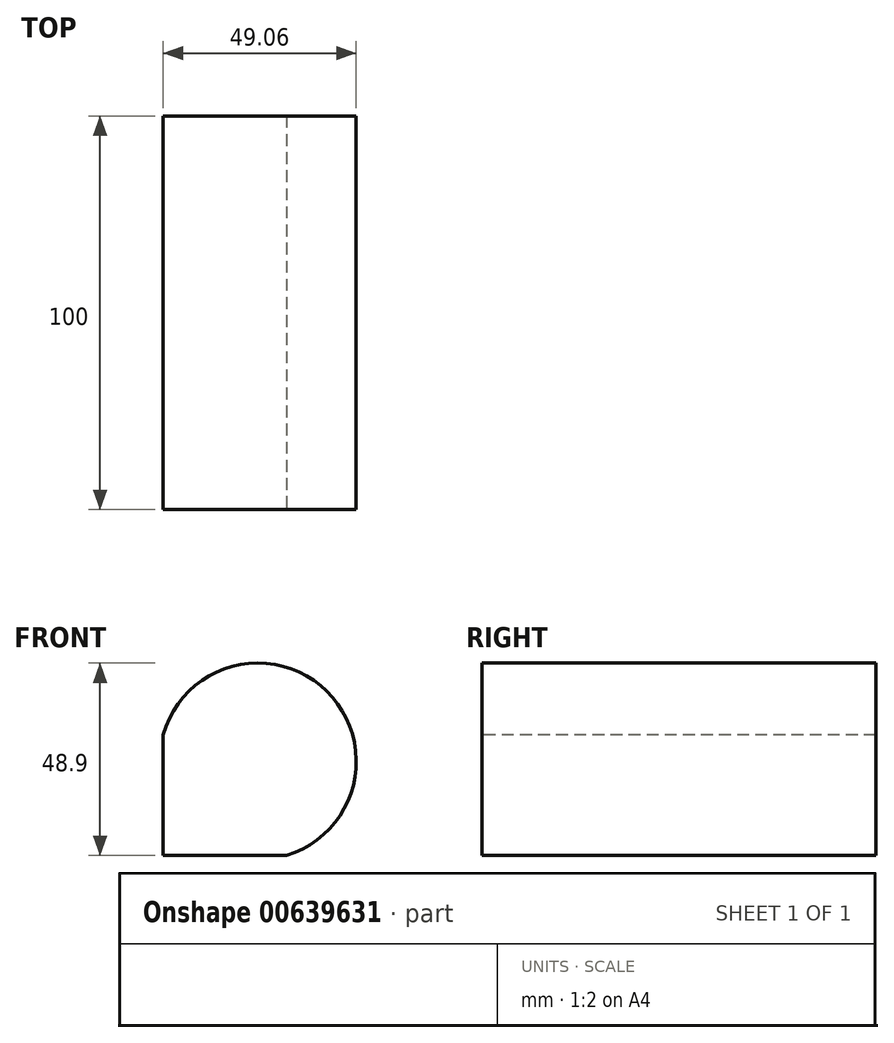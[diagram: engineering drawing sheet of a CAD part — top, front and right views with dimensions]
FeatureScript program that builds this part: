
annotation { "Feature Type Name" : "Feature", "Feature Type Description" : "" }
export const myFeature = defineFeature(function(context is Context, id is Id, definition is map)
    precondition{}
    {
        {
            var Q0;
            Q0=qCreatedBy(makeId("Top.planeOp"),FACE);
            var sketch = newSketch(context, id + "F0", { "sketchPlane" : qUnion([Q0])});
            skLineSegment(sketch, "E0.bottom", {"start": v(-50, 50) * mm, "end": v(50, 50) * mm});
            skLineSegment(sketch, "E0.top", {"start": v(-50, -50) * mm, "end": v(50, -50) * mm});
            skLineSegment(sketch, "E0.left", {"start": v(-50, 50) * mm, "end": v(-50, -50) * mm});
            skLineSegment(sketch, "E0.right", {"start": v(50, 50) * mm, "end": v(50, -50) * mm});
            skSolve(sketch);
        }
        {
            var Q0;
            Q0=makeQuery(id+"F0.imprint","IMPRINT",FACE,{"disambiguationData":[TD([[makeQuery(id+"F0.imprint","IMPRINT",EDGE,{"derivedFrom":sQuery(id+"F0.wireOp",EDGE,"E0.bottom")}),-1.0]])]});
            extrude(context, id + "F1", {"entities" : qUnion([Q0]), "depth" : 100 * mm, "offsetDistance" : 25 * mm});
        }
        {
            var Q0;
            Q0=makeQuery(id+"F1.opExtrude","SWEPT_FACE",FACE,{"disambiguationData":[OSD([sQuery(id+"F0.wireOp",EDGE,"E0.top")])]});
            var sketch = newSketch(context, id + "F2", { "sketchPlane" : qUnion([Q0])});
            skCircle(sketch, "E1", {"center": v(-36.85, 87.35) * mm, "radius": 12.5 * mm});
            skCircle(sketch, "E2", {"center": v(26.27, 58.93) * mm, "radius": 15 * mm});
            skCircle(sketch, "E3", {"center": v(-25.94, 23.9) * mm, "radius": 25 * mm});
            skSolve(sketch);
        }
        {
            var Q0;
            Q0=makeQuery(id+"F2.imprint","IMPRINT",FACE,{"disambiguationData":[TD([[makeQuery(id+"F2.imprint","IMPRINT",EDGE,{"derivedFrom":sQuery(id+"F2.wireOp",EDGE,"E1")}),1.0]])]});
            var Q1;
            {var subQ0=sQuery(id+"F2.wireOp",EDGE,"E3");var subQ1=sQuery(id+"F0.wireOp",EDGE,"E0.top");var subQ4=makeQuery(id+"F1.opExtrude","CAP_EDGE",EDGE,{"disambiguationData":[OSD([subQ1])],"isStart":true});var subQ5=makeQuery(id+"F2.imprint","INTERSECT",VERTEX,{"disambiguationData":[OD(0.0)],"derivedFrom":[subQ4,subQ0]});Q1=makeQuery(id+"F2.imprint","IMPRINT",FACE,{"disambiguationData":[TD([[makeQuery(id+"F2.imprint","IMPRINT",EDGE,{"disambiguationData":[TD([[subQ5,-1.0]])],"derivedFrom":subQ4}),1.0]])]});}
            var Q2;
            Q2=makeQuery(id+"F2.imprint","IMPRINT",FACE,{"disambiguationData":[TD([[makeQuery(id+"F2.imprint","IMPRINT",EDGE,{"derivedFrom":sQuery(id+"F2.wireOp",EDGE,"E2")}),1.0]])]});
            extrude(context, id + "F3", {"entities" : qUnion([Q0, Q1, Q2]), "operationType" : NewBodyOperationType.REMOVE, "endBound" : BoundingType.THROUGH_ALL, "oppositeDirection" : true, "depth" : 25 * mm, "offsetDistance" : 25 * mm});
        }
        {
            var Q0;
            {var subQ0=sQuery(id+"F0.wireOp",EDGE,"E0.right");var subQ3=sQuery(id+"F0.wireOp",EDGE,"E0.bottom");Q0=makeQuery(id+"F3.boolean.opBoolean","SPLIT",FACE,{"disambiguationData":[TD([makeQuery(id+"F1.opExtrude","SWEPT_FACE",FACE,{"disambiguationData":[OSD([subQ0])]})])],"derivedFrom":makeQuery(id+"F1.opExtrude","SWEPT_FACE",FACE,{"disambiguationData":[OSD([subQ3])]})});}
            cPlane(context, id + "F4", {"entities" : qUnion([Q0]), "cplaneType" : CPlaneType.OFFSET, "offset" : 50 * mm, "width" : 150 * mm, "height" : 150 * mm});
        }
        {
            var Q0;
            Q0=qCreatedBy(id+"F4.planeOp",FACE);
            cPlane(context, id + "F5", {"entities" : qUnion([Q0]), "cplaneType" : CPlaneType.OFFSET, "offset" : 50 * mm, "width" : 150 * mm, "height" : 150 * mm});
        }
        {
            var Q0;
            Q0=qCreatedBy(id+"F5.planeOp",FACE);
            cPlane(context, id + "F6", {"entities" : qUnion([Q0]), "cplaneType" : CPlaneType.OFFSET, "offset" : 50 * mm, "width" : 150 * mm, "height" : 150 * mm});
        }
        {
            var Q0;
            Q0=qCreatedBy(id+"F6.planeOp",FACE);
            cPlane(context, id + "F7", {"entities" : qUnion([Q0]), "cplaneType" : CPlaneType.OFFSET, "offset" : 50 * mm, "width" : 150 * mm, "height" : 150 * mm});
        }
    });
